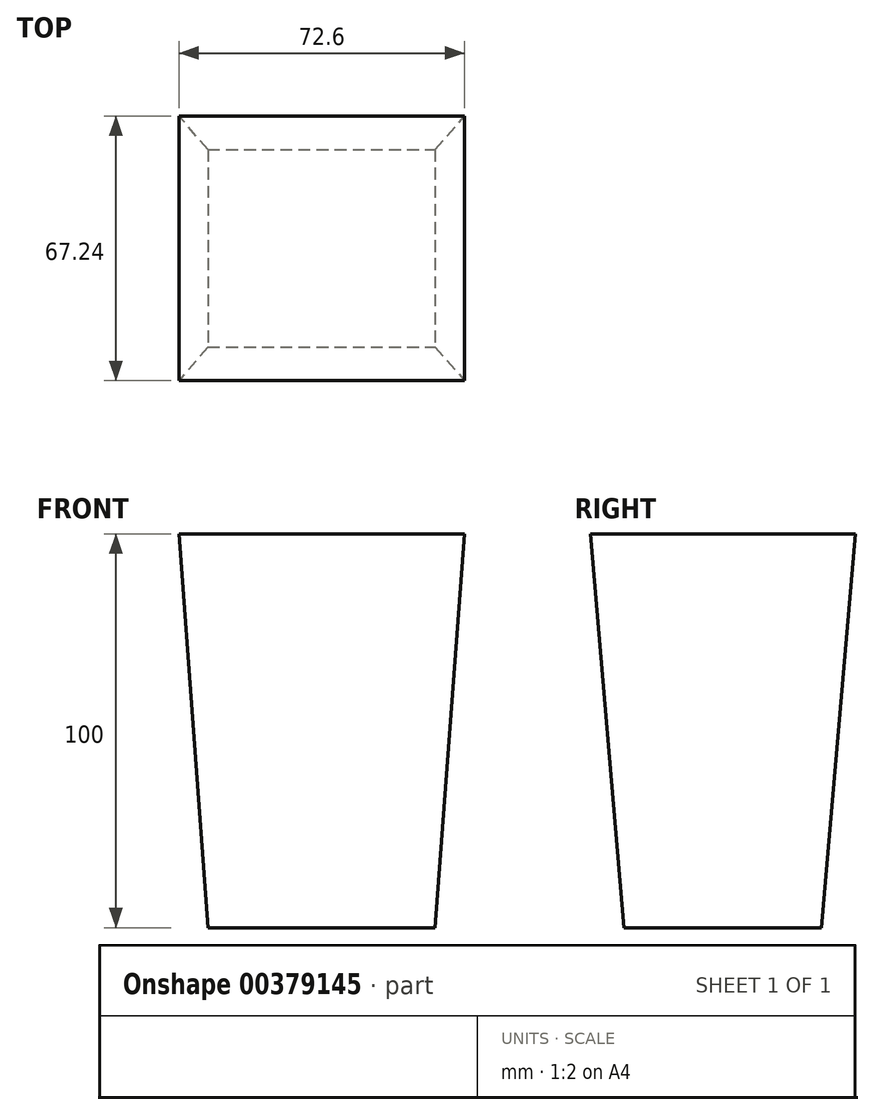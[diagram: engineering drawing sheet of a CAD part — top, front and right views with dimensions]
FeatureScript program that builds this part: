
annotation { "Feature Type Name" : "Feature", "Feature Type Description" : "" }
export const myFeature = defineFeature(function(context is Context, id is Id, definition is map)
    precondition{}
    {
        {
            var Q0;
            Q0=qCreatedBy(makeId("Top.planeOp"),FACE);
            cPlane(context, id + "F0", {"entities" : qUnion([Q0]), "cplaneType" : CPlaneType.OFFSET, "offset" : 100 * mm, "width" : 150 * mm, "height" : 150 * mm});
        }
        {
            var Q0;
            Q0=qCreatedBy(makeId("Top.planeOp"),FACE);
            var sketch = newSketch(context, id + "F1", { "sketchPlane" : qUnion([Q0])});
            skLineSegment(sketch, "E0.bottom", {"start": v(-28.93, 25.05) * mm, "end": v(28.79, 25.05) * mm});
            skLineSegment(sketch, "E0.top", {"start": v(-28.93, -25.13) * mm, "end": v(28.79, -25.13) * mm});
            skLineSegment(sketch, "E0.left", {"start": v(-28.93, 25.05) * mm, "end": v(-28.93, -25.13) * mm});
            skLineSegment(sketch, "E0.right", {"start": v(28.79, 25.05) * mm, "end": v(28.79, -25.13) * mm});
            skSolve(sketch);
        }
        {
            var Q0;
            Q0=qCreatedBy(id+"F0.planeOp",FACE);
            var sketch = newSketch(context, id + "F2", { "sketchPlane" : qUnion([Q0])});
            skLineSegment(sketch, "E1.bottom", {"start": v(-36.3, 33.62) * mm, "end": v(36.3, 33.62) * mm});
            skLineSegment(sketch, "E1.top", {"start": v(-36.3, -33.62) * mm, "end": v(36.3, -33.62) * mm});
            skLineSegment(sketch, "E1.left", {"start": v(-36.3, 33.62) * mm, "end": v(-36.3, -33.62) * mm});
            skLineSegment(sketch, "E1.right", {"start": v(36.3, 33.62) * mm, "end": v(36.3, -33.62) * mm});
            skPoint(sketch, "E1.middle", {"position": v(0, 0) * mm});
            skSolve(sketch);
        }
        {
            var Q0;
            Q0 = qSketchRegion(id + "F1", true);
            var Q1;
            Q1 = qSketchRegion(id + "F2", true);
            loft(context, id + "F3", {"sheetProfilesArray" : [{ "sheetProfileEntities" : qUnion([Q0]) }, { "sheetProfileEntities" : qUnion([Q1]) }]});
        }
    });
